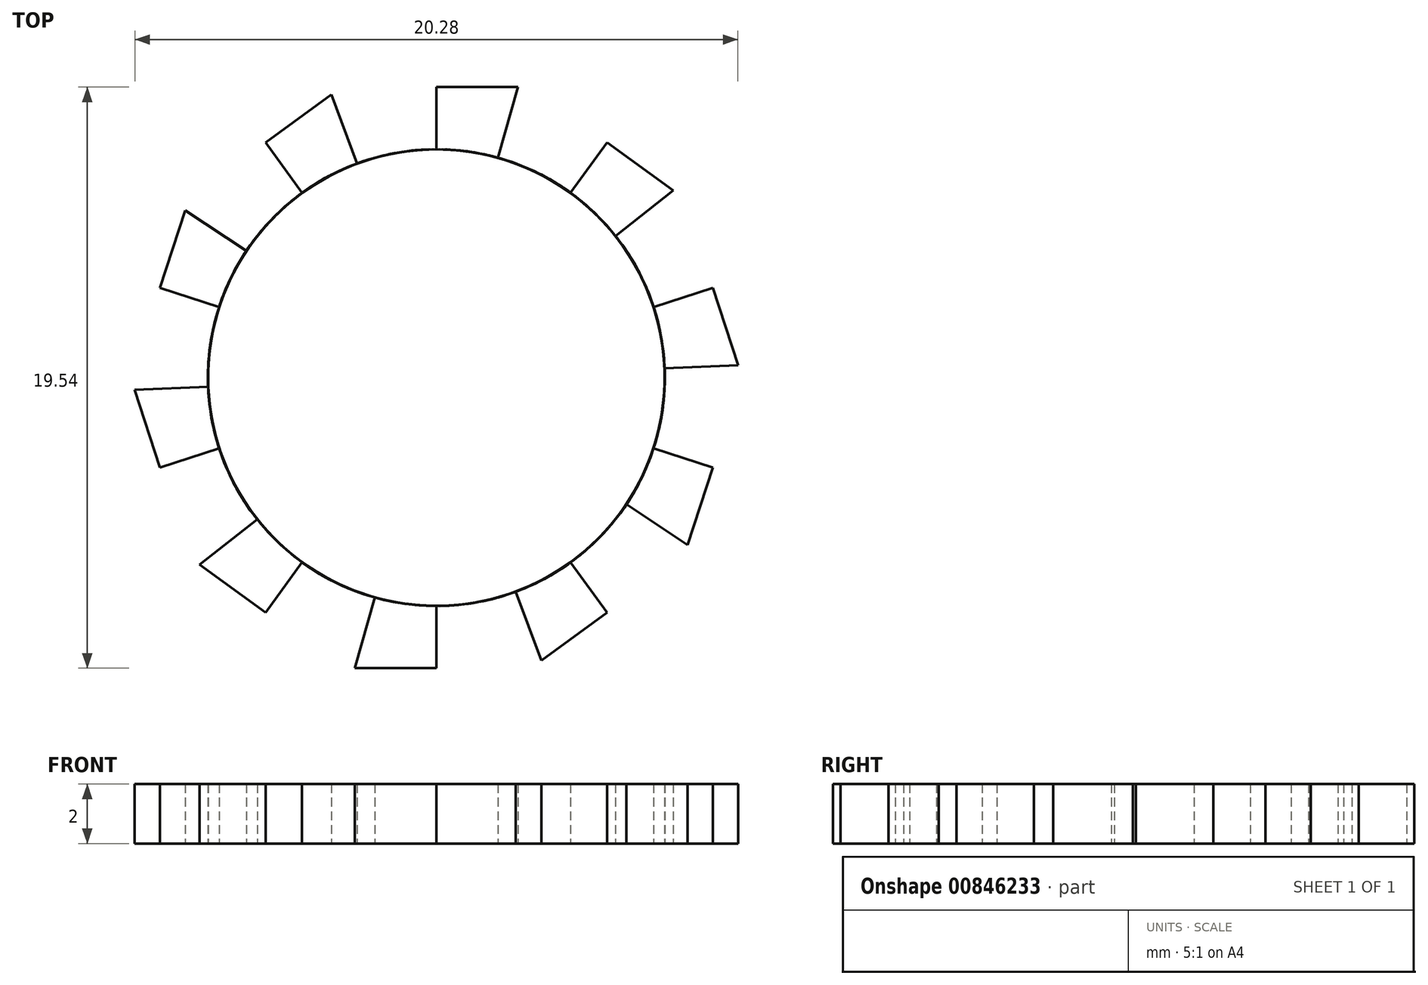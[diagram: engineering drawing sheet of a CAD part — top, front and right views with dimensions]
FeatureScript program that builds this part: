
annotation { "Feature Type Name" : "Feature", "Feature Type Description" : "" }
export const myFeature = defineFeature(function(context is Context, id is Id, definition is map)
    precondition{}
    {
        {
            var Q0;
            Q0=qCreatedBy(makeId("Top.planeOp"),FACE);
            var sketch = newSketch(context, id + "F0", { "sketchPlane" : qUnion([Q0])});
            skCircle(sketch, "E0", {"center": v(0, 0) * mm, "radius": 7.68 * mm});
            skLineSegment(sketch, "E1", {"start": v(0, 0) * mm, "end": v(0, 9.77) * mm});
            skLineSegment(sketch, "E2", {"start": v(0, 0) * mm, "end": v(2.74, 9.77) * mm});
            skLineSegment(sketch, "E3", {"start": v(2.74, 9.77) * mm, "end": v(0, 9.77) * mm});
            skSolve(sketch);
        }
        {
            var Q0;
            Q0 = qSketchRegion(id + "F0", true);
            extrude(context, id + "F1", {"entities" : qUnion([Q0]), "depth" : 2 * mm, "offsetDistance" : 25 * mm});
        }
        {
            var Q0;
            Q0=makeQuery(id+"F1.opExtrude","SWEPT_BODY",BODY,{"disambiguationData":[OSD([sQuery(id+"F0.wireOp",EDGE,"E0"),sQuery(id+"F0.wireOp",EDGE,"E1"),sQuery(id+"F0.wireOp",EDGE,"E2"),sQuery(id+"F0.wireOp",EDGE,"E3")])]});
            var Q1;
            Q1=makeQuery(id+"F1.opExtrude","SWEPT_FACE",FACE,{"disambiguationData":[OSD([sQuery(id+"F0.wireOp",EDGE,"E0")])]});
            circularPattern(context, id + "F2", {"entities" : qUnion([Q0]), "axis" : qUnion([Q1]), "angle" : 360 * degree, "instanceCount" : 10, "equalSpace" : true});
        }
    });
